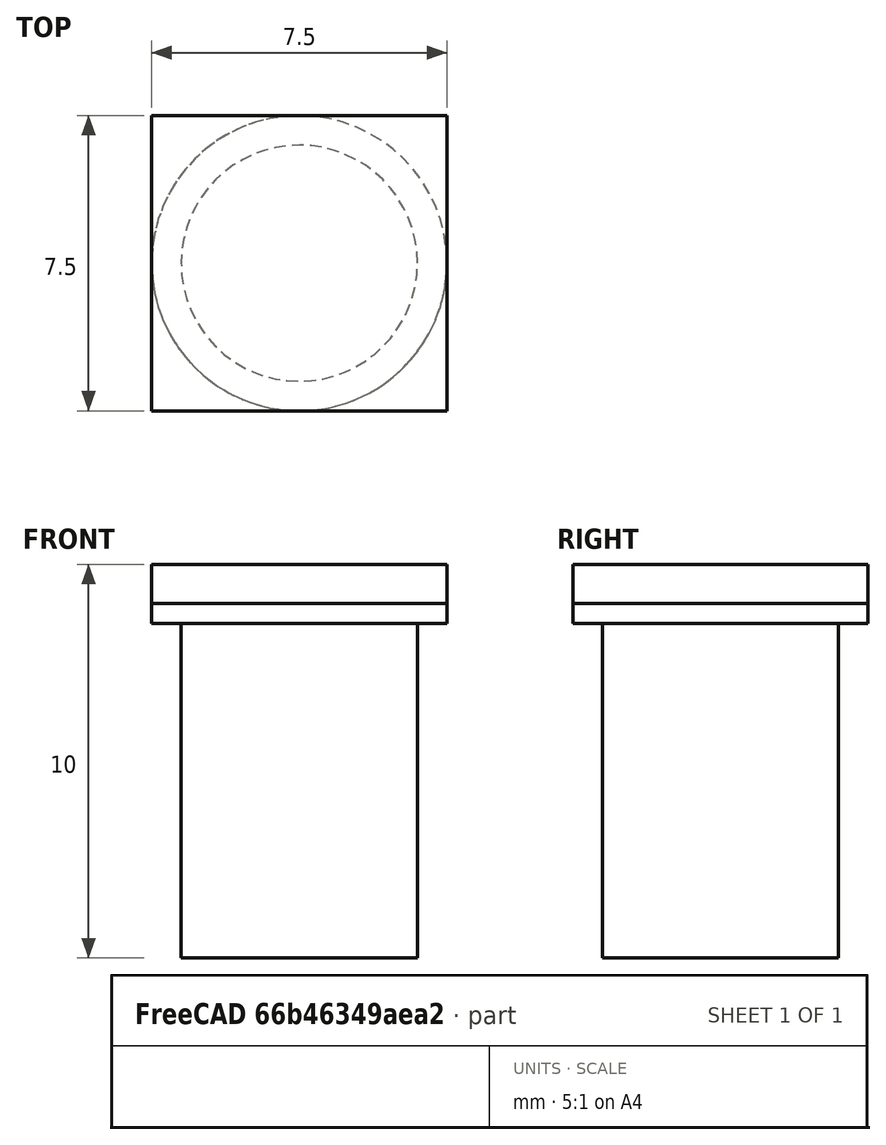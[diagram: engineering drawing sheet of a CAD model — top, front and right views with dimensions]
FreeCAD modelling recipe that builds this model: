
FCSTD DOCUMENT  (FreeCAD 0.17R13522 (Git))
Label: perforador_led_4mm
License: CreativeCommons Attribution-ShareAlike
LicenseURL: http://creativecommons.org/licenses/by-sa/4.0/
objects: Part::Part2DObjectPython×2, Part::Extrusion×2, Part::Fuse×2, Part::Box×1
note: 7 computed .brp shape members not serialized (recipe doc carries the construction recipe); baked Part::Feature solids carry a one-line shape summary decoded from their .brp

FEATURE [Part::Box] Box  label="base"
  AttacherType = Attacher::AttachEngine3D
  Height = 1
  Length = 7.5
  Width = 7.5
FEATURE [Part::Part2DObjectPython] Circle  label="circulo exterior diametro 7.5"  # Draft 2D object (typed FeaturePython)
  FirstAngle = 0
  LastAngle = 0
  MakeFace = true
  Placement = pos=(3.75,3.75,1) rot=(0,0,1;3.14159rad)
  Radius = 3.75
FEATURE [Part::Part2DObjectPython] Circle001  label="circulo inerior diametro 6"  # Draft 2D object (typed FeaturePython)
  FirstAngle = 0
  LastAngle = 0
  MakeFace = true
  Placement = pos=(3.75,3.75,1) rot=(0,0,1;3.14159rad)
  Radius = 3
FEATURE [Part::Extrusion] Extrude  label="Extrude interior pasante"
  Base = -> Circle001
  Dir = (0,0,1)
  DirMode = 2
  FaceMakerClass = Part::FaceMakerBullseye
  LengthFwd = 10
  LengthRev = 0
  Placement = pos=(0,0,-10) rot=(0,0,1;0rad)
  Solid = false
  Symmetric = false
FEATURE [Part::Extrusion] Extrude001  label="Extrude001 perfora 0.5"
  Base = -> Circle
  Dir = (0,0,1)
  DirMode = 2
  FaceMakerClass = Part::FaceMakerBullseye
  LengthFwd = 1.5
  LengthRev = 0
  Placement = pos=(0,0,-1.5) rot=(0,0,1;0rad)
  Solid = false
  Symmetric = false
FEATURE [Part::Fuse] Fusion
  Base = -> Extrude
  Refine = true
  Tool = -> Extrude001
FEATURE [Part::Fuse] Fusion001  label="perforador led 4 mm"
  Base = -> Box
  Refine = true
  Tool = -> Fusion
